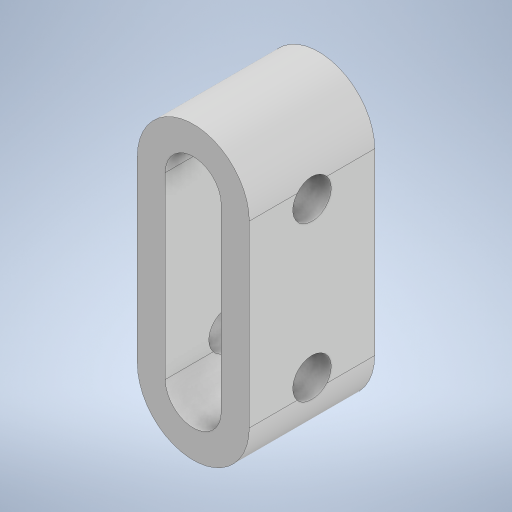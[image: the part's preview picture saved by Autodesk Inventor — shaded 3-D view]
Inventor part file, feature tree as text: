
AUTODESK INVENTOR PART (.ipt)
format: ipt  version: 2023.2 (Build 272271030, 271C)  size: 260,096 bytes
history: native  units: mm
features: extrude x2, sketch x2, plane x1, projected_geometry x1
ambient origin geometry x8: Origin, YZ Plane, XZ Plane, XY Plane, X Axis, Y Axis, Z Axis, Center Point
bodies: Solid1 (feature_tree)
feature tree (6):
  extrude  "Extrusion1"  Depth=12.5mm
  plane  "Work Plane1"
  extrude  "Extrusion2"  Depth=28.0mm TaperAngle=0.0deg
  sketch  "Sketch1"  dims[d0=40.0mm d1=12.5mm]
  sketch  "Sketch2"  dims[d2=12.5mm d3=28.0mm d4=0.0mm d5=12.5mm d6=8.6mm d7=2.75mm d8=28.0mm d9=0.0mm]
  projected_geometry  "Projected Loop1"
